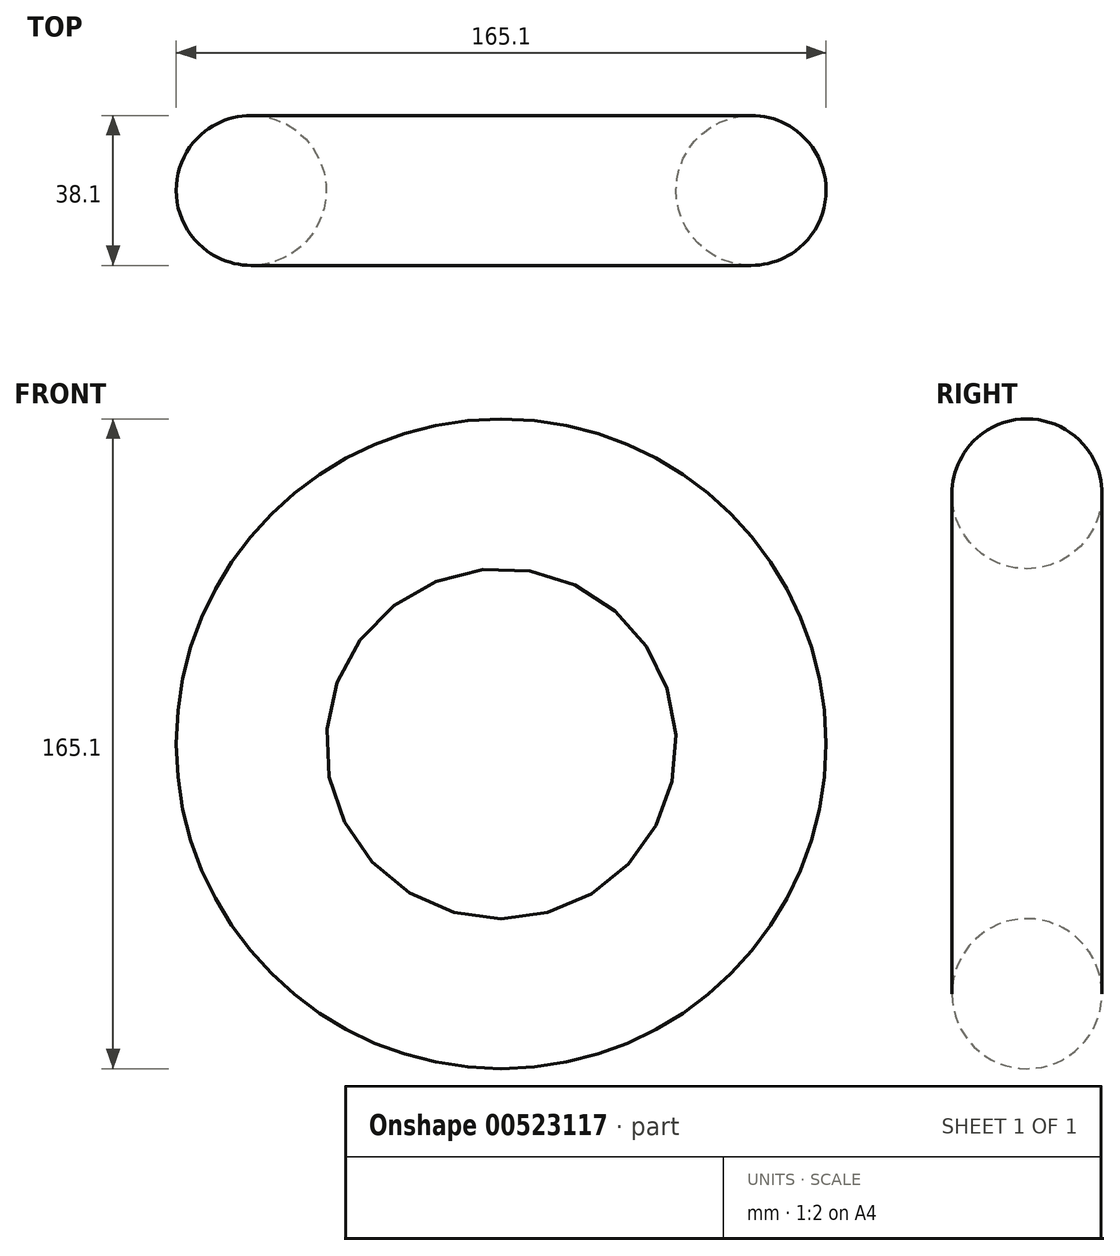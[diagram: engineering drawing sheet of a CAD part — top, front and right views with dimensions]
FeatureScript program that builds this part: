
annotation { "Feature Type Name" : "Feature", "Feature Type Description" : "" }
export const myFeature = defineFeature(function(context is Context, id is Id, definition is map)
    precondition{}
    {
        {
            var Q0;
            Q0=qCreatedBy(makeId("Top.planeOp"),FACE);
            var sketch = newSketch(context, id + "F0", { "sketchPlane" : qUnion([Q0])});
            skCircle(sketch, "E0", {"center": v(63.5, 0) * mm, "radius": 19.05 * mm});
            skLineSegment(sketch, "E1", {"start": v(0, 0) * mm, "end": v(0, 48.06) * mm, "construction": true});
            skSolve(sketch);
        }
        {
            var Q0;
            Q0=makeQuery(id+"F0.imprint","IMPRINT",FACE,{"disambiguationData":[TD([[makeQuery(id+"F0.imprint","IMPRINT",EDGE,{"derivedFrom":sQuery(id+"F0.wireOp",EDGE,"E0")}),1.0]])]});
            var Q1;
            Q1=sQuery(id+"F0.wireOp",EDGE,"E1");
            revolve(context, id + "F1", {"entities" : qUnion([Q0]), "axis" : qUnion([Q1]), "revolveType" : RevolveType.FULL});
        }
    });
